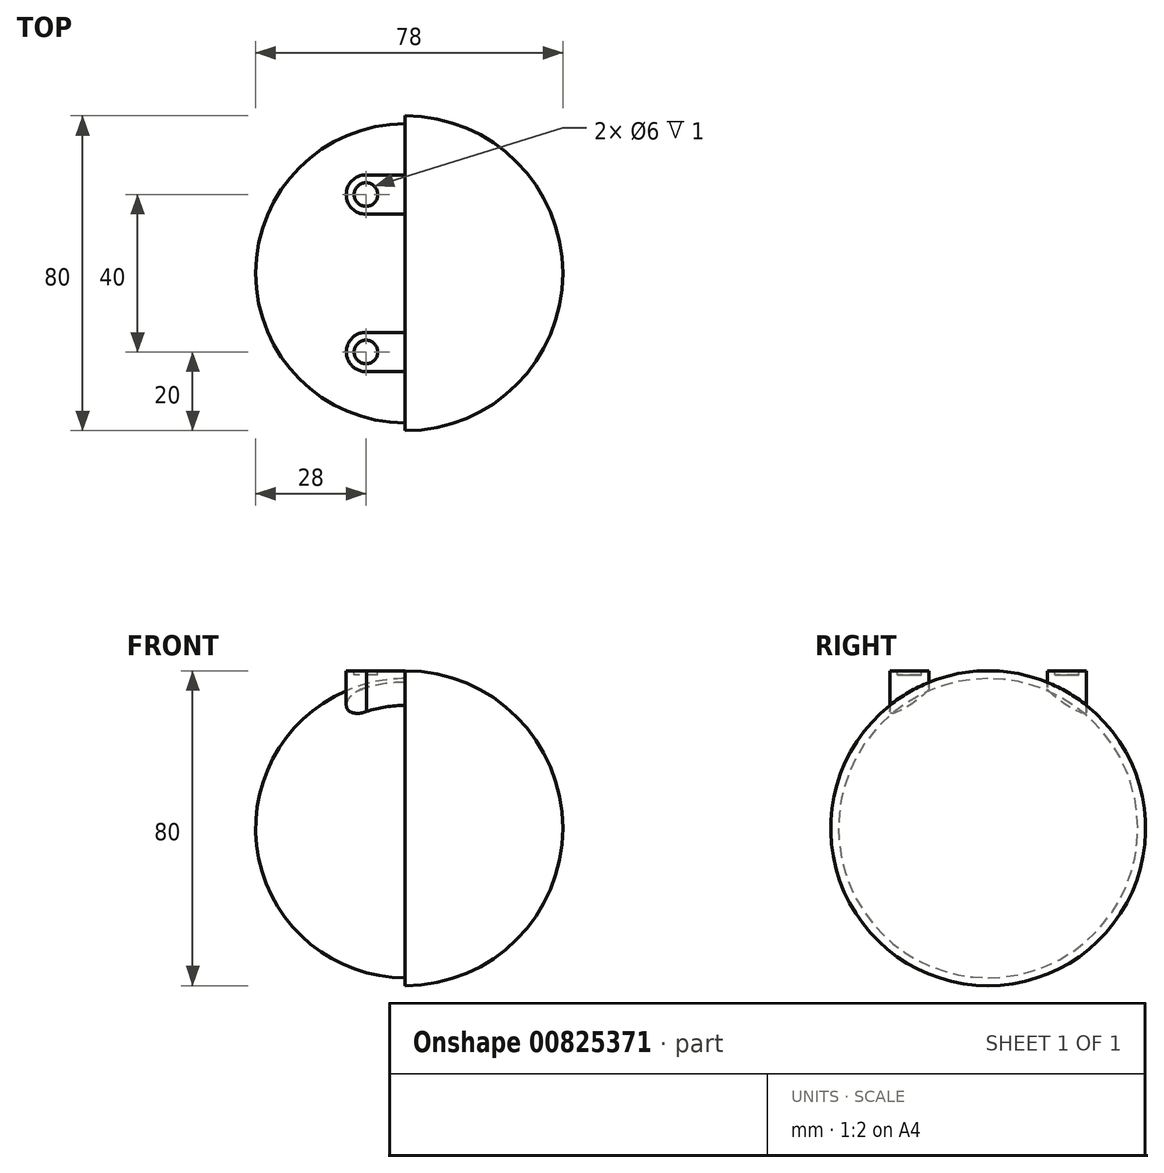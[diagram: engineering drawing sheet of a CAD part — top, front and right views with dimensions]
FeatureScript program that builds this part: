
annotation { "Feature Type Name" : "Feature", "Feature Type Description" : "" }
export const myFeature = defineFeature(function(context is Context, id is Id, definition is map)
    precondition{}
    {
        {
            var Q0;
            Q0=qCreatedBy(makeId("Front.planeOp"),FACE);
            var sketch = newSketch(context, id + "F0", { "sketchPlane" : qUnion([Q0])});
            skArc(sketch, "E0", {"start": v(0, 40) * mm, "mid": v(-40, 0) * mm, "end": v(0, -40) * mm});
            skLineSegment(sketch, "E1", {"start": v(0, 40) * mm, "end": v(0, -40) * mm});
            skSolve(sketch);
        }
        {
            var Q0;
            Q0 = qSketchRegion(id + "F0", true);
            var Q1;
            Q1=sQuery(id+"F0.wireOp",EDGE,"E1");
            revolve(context, id + "F1", {"surfaceOperationType" : NewSurfaceOperationType.NEW, "entities" : qUnion([Q0]), "axis" : qUnion([Q1]), "revolveType" : RevolveType.SYMMETRIC, "angle" : 180 * degree});
        }
        {
            var Q0;
            Q0=qCreatedBy(makeId("Top.planeOp"),FACE);
            cPlane(context, id + "F2", {"entities" : qUnion([Q0]), "cplaneType" : CPlaneType.OFFSET, "offset" : 40 * mm, "width" : 150 * mm, "height" : 150 * mm});
        }
        {
            var Q0;
            Q0=qCreatedBy(id+"F2.planeOp",FACE);
            var sketch = newSketch(context, id + "F3", { "sketchPlane" : qUnion([Q0])});
            skLineSegment(sketch, "E2", {"start": v(0, 0) * mm, "end": v(0, 20) * mm, "construction": true});
            skLineSegment(sketch, "E3", {"start": v(0, 0) * mm, "end": v(0, -20) * mm, "construction": true});
            skLineSegment(sketch, "E4", {"start": v(0, 20) * mm, "end": v(-10, 20) * mm, "construction": true});
            skLineSegment(sketch, "E5", {"start": v(0, -20) * mm, "end": v(-10, -20) * mm, "construction": true});
            skArc(sketch, "E6", {"start": v(-10, 25) * mm, "mid": v(-15, 20) * mm, "end": v(-10, 15) * mm});
            skArc(sketch, "E7", {"start": v(-9.88, -15) * mm, "mid": v(-15, -20) * mm, "end": v(-9.88, -25) * mm});
            skLineSegment(sketch, "E8", {"start": v(-10, 15) * mm, "end": v(0, 15) * mm});
            skLineSegment(sketch, "E9", {"start": v(-10, 25) * mm, "end": v(0, 25) * mm});
            skLineSegment(sketch, "E10", {"start": v(0, 25) * mm, "end": v(0, 15) * mm});
            skLineSegment(sketch, "E11", {"start": v(-9.88, -25) * mm, "end": v(0, -25) * mm});
            skLineSegment(sketch, "E12", {"start": v(-9.88, -15) * mm, "end": v(0, -15) * mm});
            skPoint(sketch, "E12.endSnap0", {"position": v(0, -10) * mm});
            skLineSegment(sketch, "E13", {"start": v(0, -15) * mm, "end": v(0, -25) * mm});
            skSolve(sketch);
        }
        {
            var Q0;
            Q0 = qSketchRegion(id + "F3", true);
            extrude(context, id + "F4", {"entities" : qUnion([Q0]), "operationType" : NewBodyOperationType.ADD, "oppositeDirection" : true, "depth" : 20 * mm, "offsetDistance" : 25 * mm});
        }
        {
            var Q0;
            Q0=makeQuery(id+"F4.opExtrude","CAP_FACE",FACE,{"disambiguationData":[OSD([sQuery(id+"F3.wireOp",EDGE,"E7"),sQuery(id+"F3.wireOp",EDGE,"E11"),sQuery(id+"F3.wireOp",EDGE,"E12"),sQuery(id+"F3.wireOp",EDGE,"E13")])],"isStart":true});
            var sketch = newSketch(context, id + "F5", { "sketchPlane" : qUnion([Q0])});
            skCircle(sketch, "E14", {"center": v(-10, -20) * mm, "radius": 3 * mm});
            skLineSegment(sketch, "E15", {"start": v(0, 0) * mm, "end": v(0, 20) * mm, "construction": true});
            skLineSegment(sketch, "E16", {"start": v(0, 20) * mm, "end": v(-10, 20) * mm, "construction": true});
            skCircle(sketch, "E17", {"center": v(-10, 20) * mm, "radius": 3 * mm});
            skSolve(sketch);
        }
        {
            var Q0;
            Q0 = qSketchRegion(id + "F5", true);
            extrude(context, id + "F6", {"entities" : qUnion([Q0]), "operationType" : NewBodyOperationType.REMOVE, "oppositeDirection" : true, "depth" : 1 * mm, "offsetDistance" : 25 * mm});
        }
        {
            var Q0;
            Q0=makeQuery(id+"F4.boolean.opBoolean","MERGE",FACE,{"derivedFrom":[makeQuery(id+"F1.opRevolve","CAP_FACE",FACE,{"disambiguationData":[OSD([sQuery(id+"F0.wireOp",EDGE,"E0"),sQuery(id+"F0.wireOp",EDGE,"E1")])],"isStart":true}),makeQuery(id+"F4.opExtrude","SWEPT_FACE",FACE,{"disambiguationData":[OSD([sQuery(id+"F3.wireOp",EDGE,"E10")])]}),makeQuery(id+"F4.opExtrude","SWEPT_FACE",FACE,{"disambiguationData":[OSD([sQuery(id+"F3.wireOp",EDGE,"E13")])]})]});
            var sketch = newSketch(context, id + "F7", { "sketchPlane" : qUnion([Q0])});
            skArc(sketch, "E18", {"start": v(0, 38) * mm, "mid": v(-38, 0) * mm, "end": v(0, -38) * mm});
            skLineSegment(sketch, "E19", {"start": v(0, 38) * mm, "end": v(0, -38) * mm});
            skSolve(sketch);
        }
        {
            var Q0;
            Q0 = qSketchRegion(id + "F7", true);
            var Q1;
            Q1=sQuery(id+"F7.wireOp",EDGE,"E19");
            revolve(context, id + "F8", {"operationType" : NewBodyOperationType.REMOVE, "surfaceOperationType" : NewSurfaceOperationType.NEW, "entities" : qUnion([Q0]), "axis" : qUnion([Q1]), "revolveType" : RevolveType.FULL, "oppositeDirection" : true});
        }
    });
